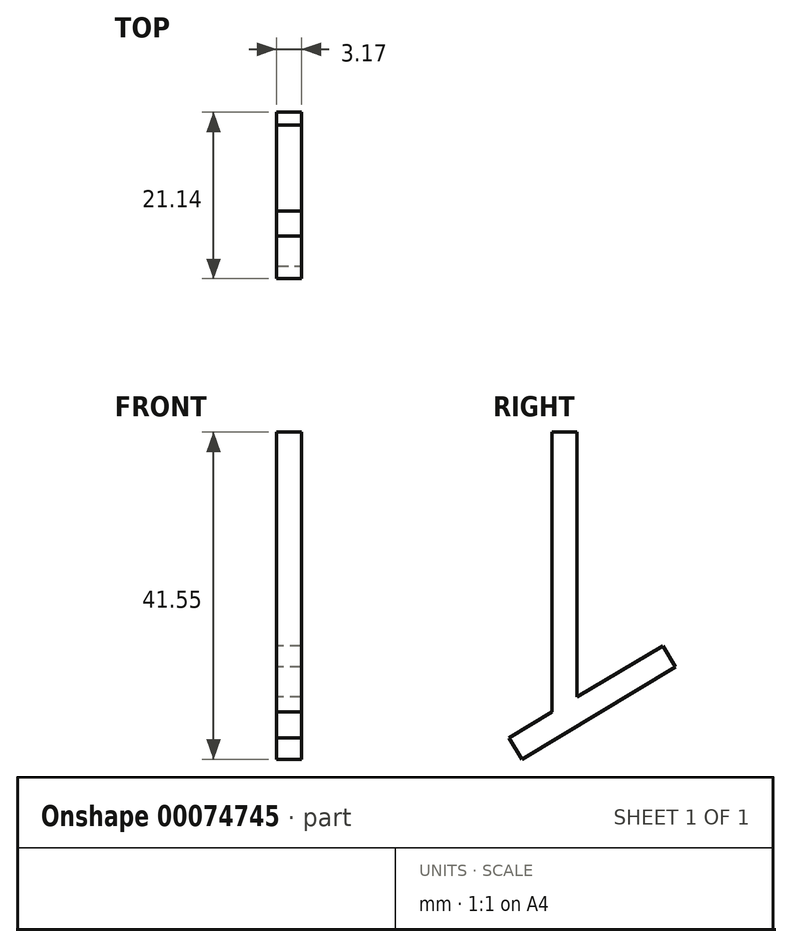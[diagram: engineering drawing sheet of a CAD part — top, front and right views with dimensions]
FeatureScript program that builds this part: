
annotation { "Feature Type Name" : "Feature", "Feature Type Description" : "" }
export const myFeature = defineFeature(function(context is Context, id is Id, definition is map)
    precondition{}
    {
        {
            var Q0;
            Q0=qCreatedBy(makeId("Front.planeOp"),FACE);
            var sketch = newSketch(context, id + "F0", { "sketchPlane" : qUnion([Q0])});
            skLineSegment(sketch, "E0", {"start": v(0, 0) * mm, "end": v(0, -35.56) * mm});
            skLineSegment(sketch, "E1", {"start": v(0, 0) * mm, "end": v(3.18, 0) * mm});
            skLineSegment(sketch, "E2", {"start": v(3.18, 0) * mm, "end": v(3.18, -35.56) * mm});
            skLineSegment(sketch, "E3", {"start": v(0, -35.56) * mm, "end": v(3.18, -35.56) * mm});
            skSolve(sketch);
        }
        {
            var Q0;
            Q0 = qSketchRegion(id + "F0", true);
            extrude(context, id + "F1", {"entities" : qUnion([Q0]), "depth" : 3.17 * mm});
        }
        {
            var Q0;
            Q0=makeQuery(id+"F1.opExtrude","CAP_EDGE",EDGE,{"disambiguationData":[OSD([sQuery(id+"F0.wireOp",EDGE,"E3")])],"isStart":true});
            chamfer(context, id + "F2", {"entities" : qUnion([Q0]), "chamferType" : ChamferType.TWO_OFFSETS, "width1" : 3.17 * mm, "oppositeDirection" : false, "width2" : 1.9 * mm, "tangentPropagation" : true});
        }
        {
            var Q0;
            Q0=makeQuery(id+"F2.opChamfer","BLEND_FACE",FACE,{"disambiguationData":[OSD([sQuery(id+"F0.wireOp",EDGE,"E3")])]});
            extrude(context, id + "F3", {"entities" : qUnion([Q0]), "depth" : 3.17 * mm});
        }
        {
            var Q0;
            {var subQ0=sQuery(id+"F0.wireOp",EDGE,"E3");var subQ1=sQuery(id+"F0.wireOp",EDGE,"E2");var subQ2=sQuery(id+"F0.wireOp",EDGE,"E1");var subQ3=sQuery(id+"F0.wireOp",EDGE,"E0");Q0=makeQuery(id+"F3.opExtrude","SWEPT_FACE",FACE,{"disambiguationData":[OSD([subQ3,subQ2,subQ1,subQ0]),TDD([makeQuery(id+"F2.opChamfer","BLEND_EDGE",EDGE,{"blendedFrom":[makeQuery(id+"F1.opExtrude","CAP_EDGE",EDGE,{"disambiguationData":[OSD([subQ0])],"isStart":true}),makeQuery(id+"F1.opExtrude","CAP_FACE",FACE,{"disambiguationData":[OSD([subQ3,subQ2,subQ1,subQ0])],"isStart":true})],"blendedInto":[makeQuery(id+"F1.opExtrude","CAP_FACE",FACE,{"disambiguationData":[OSD([subQ3,subQ2,subQ1,subQ0])],"isStart":true})]})])]});}
            extrude(context, id + "F4", {"entities" : qUnion([Q0]), "operationType" : NewBodyOperationType.ADD, "depth" : 12.7 * mm});
        }
        {
            var Q0;
            {var subQ0=sQuery(id+"F0.wireOp",EDGE,"E3");var subQ1=sQuery(id+"F0.wireOp",EDGE,"E2");var subQ2=sQuery(id+"F0.wireOp",EDGE,"E1");var subQ3=sQuery(id+"F0.wireOp",EDGE,"E0");Q0=makeQuery(id+"F3.opExtrude","SWEPT_FACE",FACE,{"disambiguationData":[OSD([subQ3,subQ2,subQ1,subQ0]),TDD([makeQuery(id+"F2.opChamfer","BLEND_EDGE",EDGE,{"blendedFrom":[makeQuery(id+"F1.opExtrude","CAP_EDGE",EDGE,{"disambiguationData":[OSD([subQ0])],"isStart":true}),makeQuery(id+"F1.opExtrude","CAP_FACE",FACE,{"disambiguationData":[OSD([subQ3,subQ2,subQ1,subQ0])],"isStart":false})],"blendedInto":[makeQuery(id+"F1.opExtrude","CAP_FACE",FACE,{"disambiguationData":[OSD([subQ3,subQ2,subQ1,subQ0])],"isStart":false})]})])]});}
            extrude(context, id + "F5", {"entities" : qUnion([Q0]), "operationType" : NewBodyOperationType.ADD, "depth" : 6.35 * mm});
        }
    });
